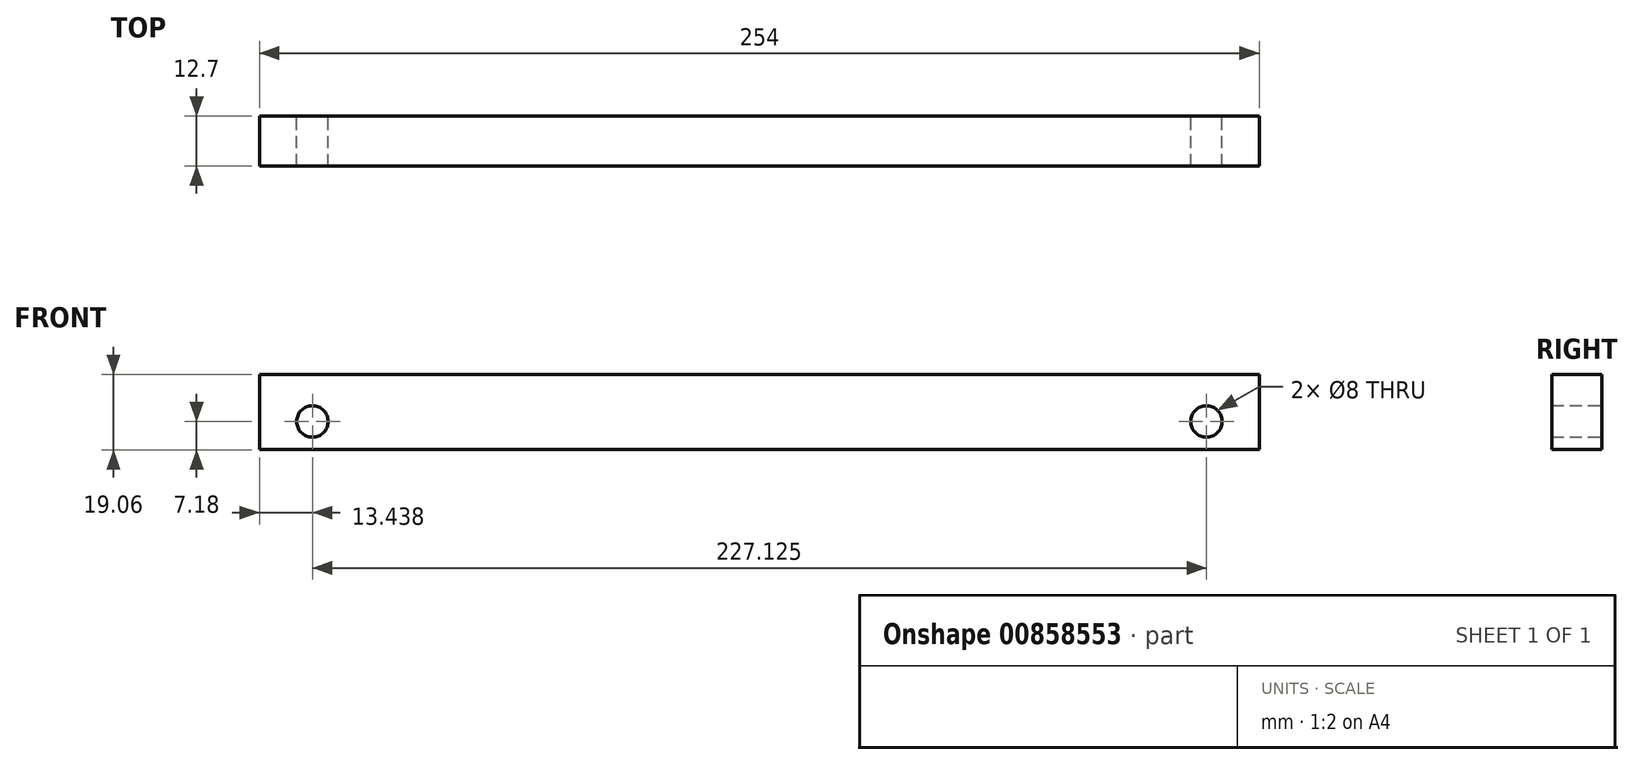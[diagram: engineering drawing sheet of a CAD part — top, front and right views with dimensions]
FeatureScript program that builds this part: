
annotation { "Feature Type Name" : "Feature", "Feature Type Description" : "" }
export const myFeature = defineFeature(function(context is Context, id is Id, definition is map)
    precondition{}
    {
        {
            var Q0;
            Q0=qCreatedBy(makeId("Front.planeOp"),FACE);
            var sketch = newSketch(context, id + "F0", { "sketchPlane" : qUnion([Q0])});
            skLineSegment(sketch, "E0", {"start": v(-113.56, 0) * mm, "end": v(113.56, 0) * mm});
            skLineSegment(sketch, "E1.bottom", {"start": v(-127, 11.87) * mm, "end": v(127, 11.87) * mm});
            skLineSegment(sketch, "E1.top", {"start": v(-127, -7.18) * mm, "end": v(127, -7.18) * mm});
            skLineSegment(sketch, "E1.left", {"start": v(-127, 11.87) * mm, "end": v(-127, -7.18) * mm});
            skLineSegment(sketch, "E1.right", {"start": v(127, 11.87) * mm, "end": v(127, -7.18) * mm});
            skPoint(sketch, "E1.middle", {"position": v(0, 0) * mm});
            skCircle(sketch, "E2", {"center": v(-113.56, 0) * mm, "radius": 4 * mm});
            skCircle(sketch, "E3", {"center": v(113.56, 0) * mm, "radius": 4 * mm});
            skSolve(sketch);
        }
        {
            var Q0;
            Q0=makeQuery(id+"F0.imprint","IMPRINT",FACE,{"disambiguationData":[TD([[makeQuery(id+"F0.imprint","IMPRINT",EDGE,{"derivedFrom":sQuery(id+"F0.wireOp",EDGE,"E1.bottom")}),-1.0]])]});
            extrude(context, id + "F1", {"entities" : qUnion([Q0]), "depth" : 12.7 * mm, "offsetDistance" : 25.4 * mm});
        }
    });
